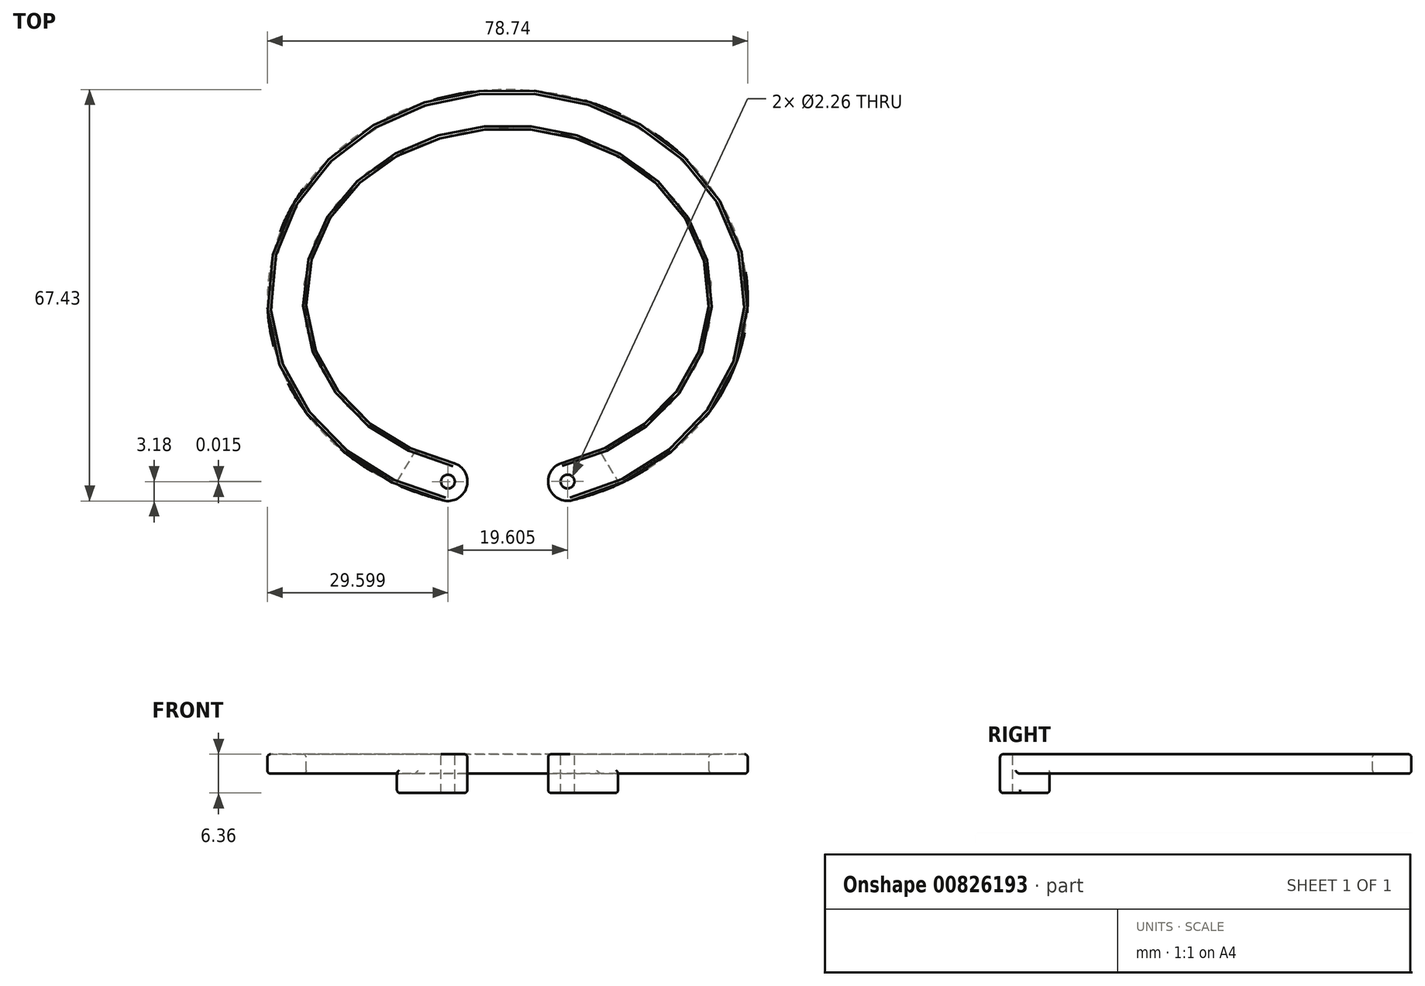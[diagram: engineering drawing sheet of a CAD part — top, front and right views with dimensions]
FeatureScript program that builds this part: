
annotation { "Feature Type Name" : "Feature", "Feature Type Description" : "" }
export const myFeature = defineFeature(function(context is Context, id is Id, definition is map)
    precondition{}
    {
        {
            var Q0;
            Q0=qCreatedBy(makeId("Top.planeOp"),FACE);
            var sketch = newSketch(context, id + "F0", { "sketchPlane" : qUnion([Q0])});
            skEllipse(sketch, "E0", {"center": v(0, 0) * mm, "majorRadius": 33.02 * mm, "minorRadius": 27.94 * mm, "majorAxis": v(1, 0)});
            skEllipse(sketch, "E1", {"center": v(0, 0) * mm, "majorRadius": 39.37 * mm, "minorRadius": 34.3 * mm, "majorAxis": v(1, 0)});
            skPoint(sketch, "E2", {"position": v(0, -27.94) * mm});
            skLineSegment(sketch, "E3", {"start": v(0, -27.94) * mm, "end": v(0, -34.3) * mm});
            skPoint(sketch, "E4", {"position": v(0, -31.12) * mm});
            skEllipse(sketch, "E5", {"center": v(0, 0) * mm, "majorRadius": 36.2 * mm, "minorRadius": 31.12 * mm, "majorAxis": v(1, 0)});
            skPoint(sketch, "E6.second.point", {"position": v(-9.77, -29.96) * mm});
            skPoint(sketch, "E7", {"position": v(9.83, -29.94) * mm});
            skLineSegment(sketch, "E8", {"start": v(0, 0) * mm, "end": v(-9.77, -29.96) * mm});
            skLineSegment(sketch, "E9", {"start": v(9.83, -29.94) * mm, "end": v(0, 0) * mm});
            skLineSegment(sketch, "E10", {"start": v(-9.77, -29.96) * mm, "end": v(-10.76, -32.99) * mm});
            skLineSegment(sketch, "E11", {"start": v(9.83, -29.94) * mm, "end": v(10.83, -32.97) * mm});
            skArc(sketch, "E12", {"start": v(-10.76, -32.99) * mm, "mid": v(-6.74, -30.95) * mm, "end": v(-8.78, -26.93) * mm});
            skArc(sketch, "E13", {"start": v(8.84, -26.92) * mm, "mid": v(6.81, -30.94) * mm, "end": v(10.83, -32.97) * mm});
            skLineSegment(sketch, "E14", {"start": v(-15.88, -26.24) * mm, "end": v(0, 0) * mm});
            skLineSegment(sketch, "E15", {"start": v(0, 0) * mm, "end": v(15.88, -26.24) * mm});
            skLineSegment(sketch, "E16", {"start": v(-15.88, -26.24) * mm, "end": v(-18.35, -30.34) * mm});
            skLineSegment(sketch, "E17", {"start": v(15.87, -26.24) * mm, "end": v(18.35, -30.34) * mm});
            skSolve(sketch);
        }
        {
            var Q0;
            {var subQ3=sQuery(id+"F0.wireOp",EDGE,"E0");var subQ6=sQuery(id+"F0.wireOp",EDGE,"E14");var subQ8=makeQuery(id+"F0.imprint","INTERSECT",VERTEX,{"derivedFrom":[subQ3,subQ6]});Q0=makeQuery(id+"F0.imprint","IMPRINT",FACE,{"disambiguationData":[TD([[makeQuery(id+"F0.imprint","IMPRINT",EDGE,{"disambiguationData":[TD([[subQ8,1.0]])],"derivedFrom":subQ3}),-1.0]])]});}
            var Q1;
            {var subQ0=sQuery(id+"F0.wireOp",EDGE,"E16");var subQ1=sQuery(id+"F0.wireOp",EDGE,"E1");var subQ2=makeQuery(id+"F0.imprint","INTERSECT",VERTEX,{"derivedFrom":[subQ1,subQ0]});Q1=makeQuery(id+"F0.imprint","IMPRINT",FACE,{"disambiguationData":[TD([[makeQuery(id+"F0.imprint","IMPRINT",EDGE,{"disambiguationData":[TD([[subQ2,1.0]])],"derivedFrom":subQ1}),1.0]])]});}
            var Q2;
            {var subQ0=sQuery(id+"F0.wireOp",EDGE,"E16");var subQ1=sQuery(id+"F0.wireOp",EDGE,"E14");var subQ2=makeQuery(id+"F0.imprint","INTERSECT",VERTEX,{"derivedFrom":[subQ1,subQ0]});Q2=makeQuery(id+"F0.imprint","IMPRINT",FACE,{"disambiguationData":[TD([[makeQuery(id+"F0.imprint","IMPRINT",EDGE,{"disambiguationData":[TD([[subQ2,-1.0]])],"derivedFrom":subQ1}),-1.0]])]});}
            var Q3;
            {var subQ0=sQuery(id+"F0.wireOp",EDGE,"E10");Q3=makeQuery(id+"F0.imprint","IMPRINT",FACE,{"disambiguationData":[TD([[makeQuery(id+"F0.imprint","IMPRINT",EDGE,{"derivedFrom":subQ0}),-1.0]])]});}
            var Q4;
            {var subQ1=sQuery(id+"F0.wireOp",EDGE,"E10");Q4=makeQuery(id+"F0.imprint","IMPRINT",FACE,{"disambiguationData":[TD([[makeQuery(id+"F0.imprint","IMPRINT",EDGE,{"derivedFrom":subQ1}),1.0]])]});}
            var Q5;
            {var subQ1=sQuery(id+"F0.wireOp",EDGE,"E5");var subQ3=sQuery(id+"F0.wireOp",EDGE,"E12");var subQ4=makeQuery(id+"F0.imprint","INTERSECT",VERTEX,{"derivedFrom":[subQ1,subQ3]});Q5=makeQuery(id+"F0.imprint","IMPRINT",FACE,{"disambiguationData":[TD([[makeQuery(id+"F0.imprint","IMPRINT",EDGE,{"disambiguationData":[TD([[subQ4,1.0]])],"derivedFrom":subQ1}),1.0]])]});}
            var Q6;
            {var subQ0=sQuery(id+"F0.wireOp",EDGE,"E17");var subQ1=sQuery(id+"F0.wireOp",EDGE,"E15");var subQ2=makeQuery(id+"F0.imprint","INTERSECT",VERTEX,{"derivedFrom":[subQ1,subQ0]});Q6=makeQuery(id+"F0.imprint","IMPRINT",FACE,{"disambiguationData":[TD([[makeQuery(id+"F0.imprint","IMPRINT",EDGE,{"disambiguationData":[TD([[subQ2,1.0]])],"derivedFrom":subQ1}),-1.0]])]});}
            var Q7;
            {var subQ0=sQuery(id+"F0.wireOp",EDGE,"E11");Q7=makeQuery(id+"F0.imprint","IMPRINT",FACE,{"disambiguationData":[TD([[makeQuery(id+"F0.imprint","IMPRINT",EDGE,{"derivedFrom":subQ0}),1.0]])]});}
            var Q8;
            {var subQ1=sQuery(id+"F0.wireOp",EDGE,"E11");Q8=makeQuery(id+"F0.imprint","IMPRINT",FACE,{"disambiguationData":[TD([[makeQuery(id+"F0.imprint","IMPRINT",EDGE,{"derivedFrom":subQ1}),-1.0]])]});}
            var Q9;
            {var subQ1=sQuery(id+"F0.wireOp",EDGE,"E5");var subQ3=sQuery(id+"F0.wireOp",EDGE,"E13");var subQ4=makeQuery(id+"F0.imprint","INTERSECT",VERTEX,{"derivedFrom":[subQ1,subQ3]});Q9=makeQuery(id+"F0.imprint","IMPRINT",FACE,{"disambiguationData":[TD([[makeQuery(id+"F0.imprint","IMPRINT",EDGE,{"disambiguationData":[TD([[subQ4,-1.0]])],"derivedFrom":subQ1}),1.0]])]});}
            extrude(context, id + "F1", {"entities" : qUnion([Q0, Q1, Q2, Q3, Q4, Q5, Q6, Q7, Q8, Q9]), "depth" : 3.17 * mm, "offsetDistance" : 25.4 * mm});
        }
        {
            var Q0;
            {var subQ0=sQuery(id+"F0.wireOp",EDGE,"E16");var subQ1=sQuery(id+"F0.wireOp",EDGE,"E14");var subQ2=makeQuery(id+"F0.imprint","INTERSECT",VERTEX,{"derivedFrom":[subQ1,subQ0]});Q0=makeQuery(id+"F0.imprint","IMPRINT",FACE,{"disambiguationData":[TD([[makeQuery(id+"F0.imprint","IMPRINT",EDGE,{"disambiguationData":[TD([[subQ2,-1.0]])],"derivedFrom":subQ1}),-1.0]])]});}
            var Q1;
            {var subQ1=sQuery(id+"F0.wireOp",EDGE,"E5");var subQ3=sQuery(id+"F0.wireOp",EDGE,"E12");var subQ4=makeQuery(id+"F0.imprint","INTERSECT",VERTEX,{"derivedFrom":[subQ1,subQ3]});Q1=makeQuery(id+"F0.imprint","IMPRINT",FACE,{"disambiguationData":[TD([[makeQuery(id+"F0.imprint","IMPRINT",EDGE,{"disambiguationData":[TD([[subQ4,1.0]])],"derivedFrom":subQ1}),1.0]])]});}
            var Q2;
            {var subQ1=sQuery(id+"F0.wireOp",EDGE,"E10");Q2=makeQuery(id+"F0.imprint","IMPRINT",FACE,{"disambiguationData":[TD([[makeQuery(id+"F0.imprint","IMPRINT",EDGE,{"derivedFrom":subQ1}),1.0]])]});}
            var Q3;
            {var subQ0=sQuery(id+"F0.wireOp",EDGE,"E10");Q3=makeQuery(id+"F0.imprint","IMPRINT",FACE,{"disambiguationData":[TD([[makeQuery(id+"F0.imprint","IMPRINT",EDGE,{"derivedFrom":subQ0}),-1.0]])]});}
            var Q4;
            {var subQ1=sQuery(id+"F0.wireOp",EDGE,"E11");Q4=makeQuery(id+"F0.imprint","IMPRINT",FACE,{"disambiguationData":[TD([[makeQuery(id+"F0.imprint","IMPRINT",EDGE,{"derivedFrom":subQ1}),-1.0]])]});}
            var Q5;
            {var subQ0=sQuery(id+"F0.wireOp",EDGE,"E11");Q5=makeQuery(id+"F0.imprint","IMPRINT",FACE,{"disambiguationData":[TD([[makeQuery(id+"F0.imprint","IMPRINT",EDGE,{"derivedFrom":subQ0}),1.0]])]});}
            var Q6;
            {var subQ0=sQuery(id+"F0.wireOp",EDGE,"E17");var subQ1=sQuery(id+"F0.wireOp",EDGE,"E15");var subQ2=makeQuery(id+"F0.imprint","INTERSECT",VERTEX,{"derivedFrom":[subQ1,subQ0]});Q6=makeQuery(id+"F0.imprint","IMPRINT",FACE,{"disambiguationData":[TD([[makeQuery(id+"F0.imprint","IMPRINT",EDGE,{"disambiguationData":[TD([[subQ2,1.0]])],"derivedFrom":subQ1}),-1.0]])]});}
            var Q7;
            {var subQ1=sQuery(id+"F0.wireOp",EDGE,"E5");var subQ3=sQuery(id+"F0.wireOp",EDGE,"E13");var subQ4=makeQuery(id+"F0.imprint","INTERSECT",VERTEX,{"derivedFrom":[subQ1,subQ3]});Q7=makeQuery(id+"F0.imprint","IMPRINT",FACE,{"disambiguationData":[TD([[makeQuery(id+"F0.imprint","IMPRINT",EDGE,{"disambiguationData":[TD([[subQ4,-1.0]])],"derivedFrom":subQ1}),1.0]])]});}
            extrude(context, id + "F2", {"entities" : qUnion([Q0, Q1, Q2, Q3, Q4, Q5, Q6, Q7]), "operationType" : NewBodyOperationType.ADD, "oppositeDirection" : true, "depth" : 3.17 * mm, "offsetDistance" : 25.4 * mm});
        }
        {
            var Q0;
            Q0=makeQuery(id+"F1.opExtrude","SWEPT_FACE",FACE,{"disambiguationData":[OSD([sQuery(id+"F0.wireOp",EDGE,"E1")])]});
            var Q1;
            Q1=makeQuery(id+"F1.opExtrude","SWEPT_FACE",FACE,{"disambiguationData":[OSD([sQuery(id+"F0.wireOp",EDGE,"E0")])]});
            var Q2;
            Q2=makeQuery(id+"F1.opExtrude","SWEPT_FACE",FACE,{"disambiguationData":[OSD([sQuery(id+"F0.wireOp",EDGE,"E12")])]});
            var Q3;
            Q3=makeQuery(id+"F1.opExtrude","SWEPT_FACE",FACE,{"disambiguationData":[OSD([sQuery(id+"F0.wireOp",EDGE,"E13")])]});
            var Q4;
            Q4=makeQuery(id+"F2.opExtrude","CAP_EDGE",EDGE,{"disambiguationData":[OSD([sQuery(id+"F0.wireOp",EDGE,"E14"),sQuery(id+"F0.wireOp",EDGE,"E16")])],"isStart":true});
            var Q5;
            Q5=makeQuery(id+"F2.opExtrude","CAP_EDGE",EDGE,{"disambiguationData":[OSD([sQuery(id+"F0.wireOp",EDGE,"E14"),sQuery(id+"F0.wireOp",EDGE,"E16")])],"isStart":false});
            var Q6;
            Q6=makeQuery(id+"F2.opExtrude","CAP_EDGE",EDGE,{"disambiguationData":[OSD([sQuery(id+"F0.wireOp",EDGE,"E15"),sQuery(id+"F0.wireOp",EDGE,"E17")])],"isStart":true});
            var Q7;
            Q7=makeQuery(id+"F2.opExtrude","CAP_EDGE",EDGE,{"disambiguationData":[OSD([sQuery(id+"F0.wireOp",EDGE,"E15"),sQuery(id+"F0.wireOp",EDGE,"E17")])],"isStart":false});
            fillet(context, id + "F3", {"entities" : qUnion([Q0, Q1, Q2, Q3, Q4, Q5, Q6, Q7]), "radius" : 0.5 * mm, "tangentPropagation" : true, "allowEdgeOverflow" : false});
        }
        {
            var Q0;
            Q0=makeQuery(id+"F1.opExtrude","CAP_FACE",FACE,{"disambiguationData":[OSD([sQuery(id+"F0.wireOp",EDGE,"E0"),sQuery(id+"F0.wireOp",EDGE,"E1"),sQuery(id+"F0.wireOp",EDGE,"E12"),sQuery(id+"F0.wireOp",EDGE,"E13")])],"isStart":false});
            var sketch = newSketch(context, id + "F4", { "sketchPlane" : qUnion([Q0])});
            skPoint(sketch, "E18.0", {"position": v(-9.77, -29.96) * mm});
            skPoint(sketch, "E18.1", {"position": v(9.83, -29.94) * mm});
            skSolve(sketch);
        }
        {
            var Q0;
            Q0=sQuery(id+"F4.wireOp",VERTEX,"E18.0");
            var Q1;
            Q1=sQuery(id+"F4.wireOp",VERTEX,"E18.1");
            var Q2;
            Q2=makeQuery(id+"F1.opExtrude","SWEPT_BODY",BODY,{"disambiguationData":[OSD([sQuery(id+"F0.wireOp",EDGE,"E0"),sQuery(id+"F0.wireOp",EDGE,"E1"),sQuery(id+"F0.wireOp",EDGE,"E12"),sQuery(id+"F0.wireOp",EDGE,"E13")])]});
            hole(context, id + "F5", {"style" : HoleStyle.SIMPLE, "endStyle" : HoleEndStyle.BLIND, "standardTappedOrClearance" : lookupTablePath({ "standard" : "ANSI", "engagement" : "75%", "pitch" : "40 tpi", "size" : "#4", "type" : "Tapped" }), "standardBlindInLast" : lookupTablePath({ "standard" : "ANSI", "engagement" : "75%", "pitch" : "40 tpi", "size" : "#4", "type" : "Tapped" }), "holeDiameter" : 2.26 * mm, "majorDiameter" : 2.84 * mm, "showTappedDepth" : true, "holeDepth" : 14.6 * mm, "isTappedThrough" : true, "tappedDepth" : 12.7 * mm, "tapClearance" : 3, "locations" : qUnion([Q0, Q1]), "scope" : qUnion([Q2])});
        }
    });
